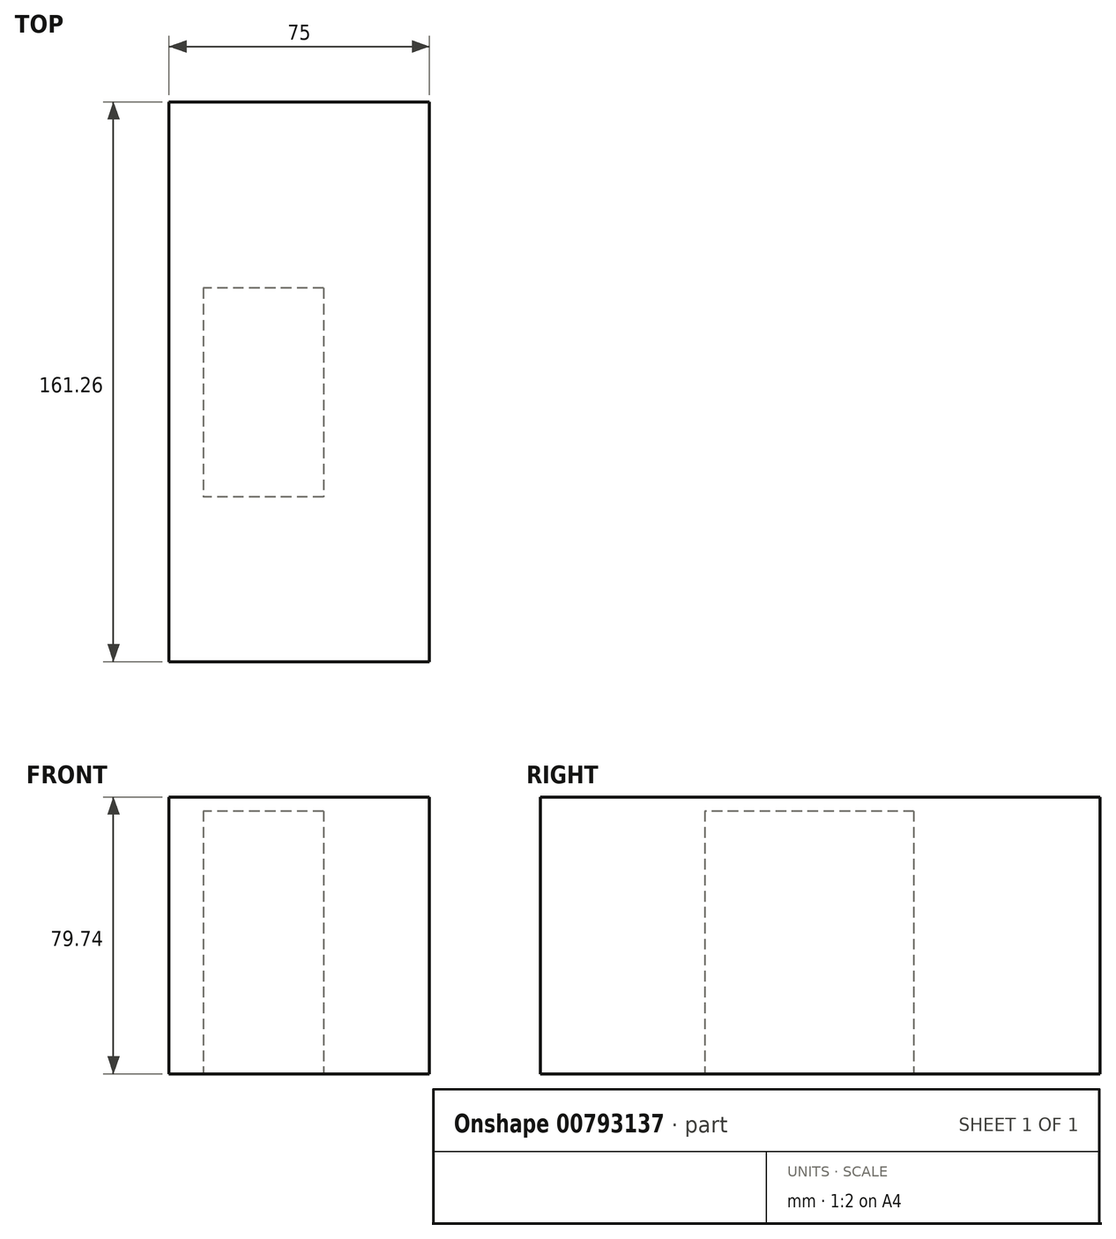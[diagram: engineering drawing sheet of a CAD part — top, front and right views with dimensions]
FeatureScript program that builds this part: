
annotation { "Feature Type Name" : "Feature", "Feature Type Description" : "" }
export const myFeature = defineFeature(function(context is Context, id is Id, definition is map)
    precondition{}
    {
        {
            var Q0;
            Q0=qCreatedBy(makeId("Right.planeOp"),FACE);
            var sketch = newSketch(context, id + "F0", { "sketchPlane" : qUnion([Q0])});
            skLineSegment(sketch, "E0.bottom", {"start": v(80.63, 39.87) * mm, "end": v(-80.63, 39.87) * mm});
            skLineSegment(sketch, "E0.top", {"start": v(80.63, -39.87) * mm, "end": v(-80.63, -39.87) * mm});
            skLineSegment(sketch, "E0.left", {"start": v(80.63, 39.87) * mm, "end": v(80.63, -39.87) * mm});
            skLineSegment(sketch, "E0.right", {"start": v(-80.63, 39.87) * mm, "end": v(-80.63, -39.87) * mm});
            skPoint(sketch, "E0.middle", {"position": v(0, 0) * mm});
            skSolve(sketch);
        }
        {
            var Q0;
            Q0=makeQuery(id+"F0.imprint","IMPRINT",FACE,{"disambiguationData":[TD([[makeQuery(id+"F0.imprint","IMPRINT",EDGE,{"derivedFrom":sQuery(id+"F0.wireOp",EDGE,"E0.bottom")}),1.0]])]});
            extrude(context, id + "F1", {"entities" : qUnion([Q0]), "depth" : 75 * mm, "offsetDistance" : 25 * mm});
        }
        {
            var Q0;
            Q0=qCreatedBy(makeId("Top.planeOp"),FACE);
            cPlane(context, id + "F2", {"entities" : qUnion([Q0]), "cplaneType" : CPlaneType.OFFSET, "offset" : 40.8 * mm, "oppositeDirection" : true, "width" : 150 * mm, "height" : 150 * mm});
        }
        {
            var Q0;
            Q0=qCreatedBy(id+"F2.planeOp",FACE);
            var sketch = newSketch(context, id + "F3", { "sketchPlane" : qUnion([Q0])});
            skLineSegment(sketch, "E1.bottom", {"start": v(44.48, 27) * mm, "end": v(9.8, 27) * mm});
            skLineSegment(sketch, "E1.top", {"start": v(44.48, -33.2) * mm, "end": v(9.8, -33.2) * mm});
            skLineSegment(sketch, "E1.left", {"start": v(44.48, 27) * mm, "end": v(44.48, -33.2) * mm});
            skLineSegment(sketch, "E1.right", {"start": v(9.8, 27) * mm, "end": v(9.8, -33.2) * mm});
            skSolve(sketch);
        }
        {
            var Q0;
            Q0=makeQuery(id+"F3.imprint","IMPRINT",FACE,{"disambiguationData":[TD([[makeQuery(id+"F3.imprint","IMPRINT",EDGE,{"derivedFrom":sQuery(id+"F3.wireOp",EDGE,"E1.bottom")}),1.0]])]});
            extrude(context, id + "F4", {"entities" : qUnion([Q0]), "operationType" : NewBodyOperationType.REMOVE, "depth" : 76.6 * mm, "offsetDistance" : 25 * mm});
        }
    });
